# Revit family: NASHIRA_200
name_source: partatom
category: Equipos mecánicos
units: mm (PartAtom-declared; Revit-internal decimal feet)

## family parameters
Clasificación = Ninguno
Compartido = No
Corte con vacíos al cargar = No
Cota de conector redondo = Usar diámetro
Mantener orientación de anotación = No
Número OmniClass = 23.75.70.14.34
Punto de cálculo de habitación = No
Se basa en plano de trabajo = Sí
Siempre vertical = No
Tipo de pieza = Normal
Título OmniClass = Air Duct Accessories

## types (4) — shared parameters
Autor = BIM6D
Aux.1 = 5 mm  [stored 0.0164042 ft]
Aux.2 = 150 mm
Aux.3 = 170 mm  [stored 0.557743 ft]
CorrienteNominal = 0 A
Elevación por defecto = 1219 mm
Exportar tipo a IFC como = IfcAirTerminalBoxType
Fabricante = S&P Sistemas de Ventilación S.L.U.
FlujoAire1 = 0.0 L/s
FlujoAire2 = 0.0 L/s
FlujoAire3 = 0.0 L/s
FlujoAire4 = 0.0 L/s
IfcExportAs = IfcAirTerminalBoxType
IfcExportType = CONSTANTFLOW
Imagen de tipo = <Ninguno>
IndiceFlujoNominal = 0.0 L/s
Introducir el tipo predefinido de IFC = CONSTANTFLOW
Material Carcasa = SP_Plastic_Grey
Material Carcasa B = SP_Plastic_White
Material Conector Bornes = SP_Plastic_Red
Modelo = NASHIRA
PA = 1000 mm  [stored 3.28084 ft]
PB = 600 mm  [stored 1.9685 ft]
PC = 210 mm  [stored 0.688976 ft]
PesoBruto = 0.00 kg
PresionDinamica = 0.0 Pa
PresionEstaticaNominal = 0.0 Pa
PresionTotalNominal = 0.0 Pa
TensionNominal = 0 V
UNSPSCCodigo = 72151204
UNSPSCTitulo = HVAC ventilation and duct work construction service
URL = https://www.solerpalau.com
URLProducto = https://easyvent.solerpalau.com
Uniclass2.0Codigo = 23.75.70.14.34
Uniclass2.0Titulo = Ductwork accessories
VelocidadRotacionNominal = 0
spIntensidadMaximaAbsorbida = 0 A
spPotenciaElectrica_Solucion = 0 W
spPotenciaUtil_Solucion = 0 W

## per-type parameters (varying)
| type | Aux.4 | Aux.5 Tapon | Diametro Conector 1 | IndicePotenciaNominal | PD | spCodigoComercialProducto | spCodigoProductoEasyvent | spTamañoVentilador |
| NASHIRA 200 E R8 | 155 mm  [stored 0.50853 ft] | 85 mm  [stored 0.278871 ft] | 160 mm  [stored 0.524934 ft] | 136 W | 160 mm  [stored 0.524934 ft] | 5153193600 | 5153193600 | 150 mm |
| NASHIRA 150 E R8 | 120 mm  [stored 0.393701 ft] | 68 mm | 125 mm  [stored 0.410105 ft] | 112 W | 125 mm  [stored 0.410105 ft] | 5153193500 | 5153193500 | 125 mm  [stored 0.410105 ft] |
| NASHIRA 200 R8 | 155 mm  [stored 0.50853 ft] | 85 mm  [stored 0.278871 ft] | 160 mm  [stored 0.524934 ft] | 136 W | 160 mm  [stored 0.524934 ft] | 5153193400 | 5153193400 | 150 mm |
| NASHIRA 150 R8 | 120 mm  [stored 0.393701 ft] | 68 mm | 125 mm  [stored 0.410105 ft] | 112 W | 125 mm  [stored 0.410105 ft] | 5153193300 | 5153193300 | 125 mm  [stored 0.410105 ft] |

note: column(s) folded — value = type name in every type: spConfiguracionProductoGenerico, spDescripcionComercialProducto, spDescripcionProductoEasyvent

note: [stored X ft] marks values corroborated as IEEE doubles in the binary element streams (Revit-internal decimal feet)

## geometry (parser evidence)
native form markers: Blend x2
no freeform markers — native parametric forms only
